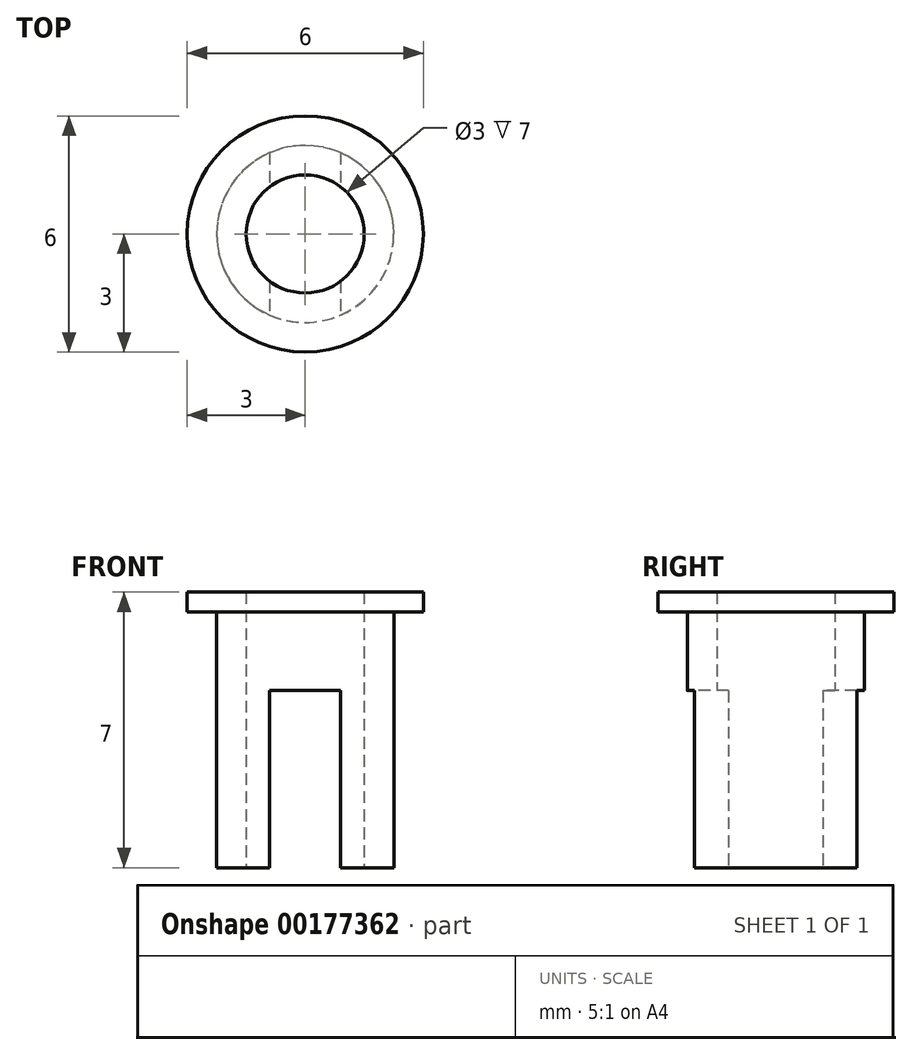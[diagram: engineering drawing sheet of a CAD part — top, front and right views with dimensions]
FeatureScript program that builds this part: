
annotation { "Feature Type Name" : "Feature", "Feature Type Description" : "" }
export const myFeature = defineFeature(function(context is Context, id is Id, definition is map)
    precondition{}
    {
        {
            var Q0;
            Q0=qCreatedBy(makeId("Front.planeOp"),FACE);
            var sketch = newSketch(context, id + "F0", { "sketchPlane" : qUnion([Q0])});
            skLineSegment(sketch, "E0", {"start": v(0, 0) * mm, "end": v(0, 4) * mm, "construction": true});
            skLineSegment(sketch, "E1", {"start": v(-1.5, 0) * mm, "end": v(-2.25, 0) * mm});
            skLineSegment(sketch, "E2", {"start": v(-2.25, 0) * mm, "end": v(-2.25, 6.5) * mm});
            skLineSegment(sketch, "E3", {"start": v(-2.25, 6.5) * mm, "end": v(-3, 6.5) * mm});
            skLineSegment(sketch, "E4", {"start": v(-3, 6.5) * mm, "end": v(-3, 7) * mm});
            skLineSegment(sketch, "E5", {"start": v(-3, 7) * mm, "end": v(-1.5, 7) * mm});
            skLineSegment(sketch, "E6", {"start": v(-1.5, 7) * mm, "end": v(-1.5, 0) * mm});
            skSolve(sketch);
        }
        {
            var Q0;
            Q0 = qSketchRegion(id + "F0", true);
            var Q1;
            Q1=sQuery(id+"F0.wireOp",EDGE,"E0");
            revolve(context, id + "F1", {"surfaceOperationType" : NewSurfaceOperationType.NEW, "entities" : qUnion([Q0]), "axis" : qUnion([Q1]), "revolveType" : RevolveType.FULL});
        }
        {
            var Q0;
            Q0=qCreatedBy(makeId("Front.planeOp"),FACE);
            var sketch = newSketch(context, id + "F2", { "sketchPlane" : qUnion([Q0])});
            skLineSegment(sketch, "E7.bottom", {"start": v(-0.9, -0.54) * mm, "end": v(0.9, -0.54) * mm});
            skLineSegment(sketch, "E7.top", {"start": v(-0.9, 4.5) * mm, "end": v(0.9, 4.5) * mm});
            skLineSegment(sketch, "E7.left", {"start": v(-0.9, -0.54) * mm, "end": v(-0.9, 4.5) * mm});
            skLineSegment(sketch, "E7.right", {"start": v(0.9, -0.54) * mm, "end": v(0.9, 4.5) * mm});
            skSolve(sketch);
        }
        {
            var Q0;
            Q0 = qSketchRegion(id + "F2", true);
            extrude(context, id + "F3", {"entities" : qUnion([Q0]), "operationType" : NewBodyOperationType.REMOVE, "oppositeDirection" : true, "depth" : 25 * mm, "offsetDistance" : 25 * mm, "symmetric" : true});
        }
    });
